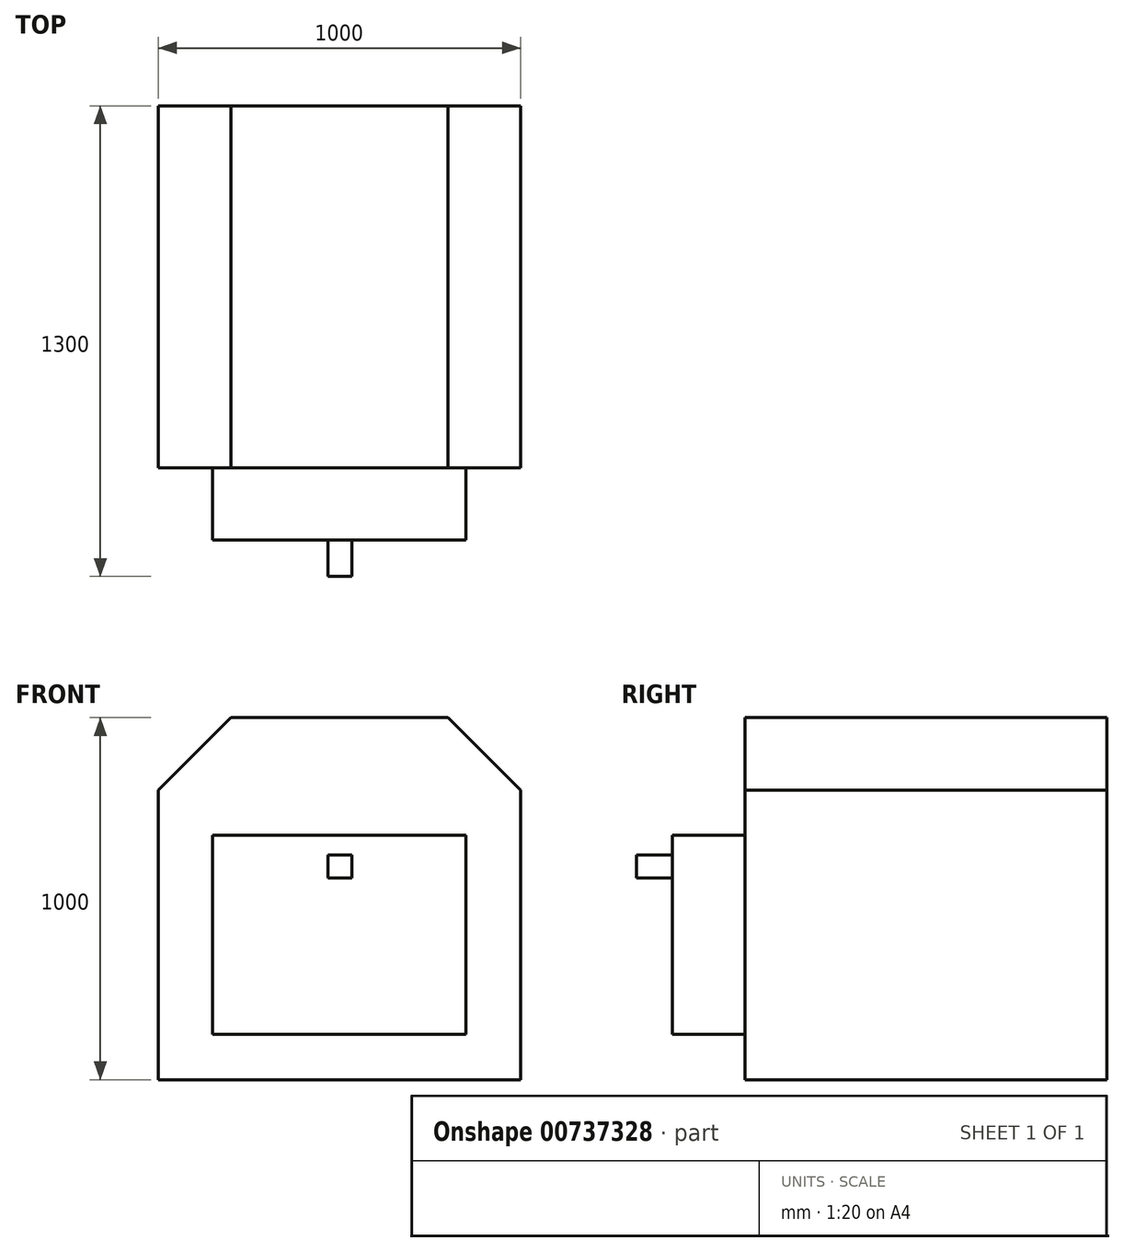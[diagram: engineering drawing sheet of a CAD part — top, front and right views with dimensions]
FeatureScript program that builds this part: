
annotation { "Feature Type Name" : "Feature", "Feature Type Description" : "" }
export const myFeature = defineFeature(function(context is Context, id is Id, definition is map)
    precondition{}
    {
        {
            var Q0;
            Q0=qCreatedBy(makeId("Front.planeOp"),FACE);
            var sketch = newSketch(context, id + "F0", { "sketchPlane" : qUnion([Q0])});
            skLineSegment(sketch, "E0.bottom", {"start": v(-500.63, 675.79) * mm, "end": v(499.37, 675.79) * mm});
            skLineSegment(sketch, "E0.top", {"start": v(-500.63, -324.21) * mm, "end": v(499.37, -324.21) * mm});
            skLineSegment(sketch, "E0.left", {"start": v(-500.63, 675.79) * mm, "end": v(-500.63, -324.21) * mm});
            skLineSegment(sketch, "E0.right", {"start": v(499.37, 675.79) * mm, "end": v(499.37, -324.21) * mm});
            skSolve(sketch);
        }
        {
            var Q0;
            Q0 = qSketchRegion(id + "F0", true);
            extrude(context, id + "F1", {"entities" : qUnion([Q0]), "depth" : 1000 * mm, "offsetDistance" : 25 * mm});
        }
        {
            var Q0;
            Q0=makeQuery(id+"F1.opExtrude","SWEPT_EDGE",EDGE,{"disambiguationData":[OSD([sQuery(id+"F0.wireOp",EDGE,"E0.bottom"),sQuery(id+"F0.wireOp",EDGE,"E0.left")])]});
            var Q1;
            Q1=makeQuery(id+"F1.opExtrude","SWEPT_EDGE",EDGE,{"disambiguationData":[OSD([sQuery(id+"F0.wireOp",EDGE,"E0.bottom"),sQuery(id+"F0.wireOp",EDGE,"E0.right")])]});
            chamfer(context, id + "F2", {"entities" : qUnion([Q0, Q1]), "width" : 200 * mm, "tangentPropagation" : true});
        }
        {
            var Q0;
            Q0=makeQuery(id+"F1.opExtrude","CAP_FACE",FACE,{"disambiguationData":[OSD([sQuery(id+"F0.wireOp",EDGE,"E0.bottom"),sQuery(id+"F0.wireOp",EDGE,"E0.top"),sQuery(id+"F0.wireOp",EDGE,"E0.left"),sQuery(id+"F0.wireOp",EDGE,"E0.right")])],"isStart":false});
            var sketch = newSketch(context, id + "F3", { "sketchPlane" : qUnion([Q0])});
            skLineSegment(sketch, "E1.bottom", {"start": v(-350.63, 350.63) * mm, "end": v(349.37, 350.63) * mm});
            skLineSegment(sketch, "E1.top", {"start": v(-350.63, -199.22) * mm, "end": v(349.37, -199.22) * mm});
            skLineSegment(sketch, "E1.left", {"start": v(-350.63, 350.63) * mm, "end": v(-350.63, -199.22) * mm});
            skLineSegment(sketch, "E1.right", {"start": v(349.37, 350.63) * mm, "end": v(349.37, -199.22) * mm});
            skSolve(sketch);
        }
        {
            var Q0;
            Q0 = qSketchRegion(id + "F3", true);
            extrude(context, id + "F4", {"entities" : qUnion([Q0]), "operationType" : NewBodyOperationType.ADD, "depth" : 200 * mm, "offsetDistance" : 25 * mm});
        }
        {
            var Q0;
            Q0=makeQuery(id+"F4.opExtrude","CAP_FACE",FACE,{"disambiguationData":[OSD([sQuery(id+"F3.wireOp",EDGE,"E1.bottom"),sQuery(id+"F3.wireOp",EDGE,"E1.top"),sQuery(id+"F3.wireOp",EDGE,"E1.left"),sQuery(id+"F3.wireOp",EDGE,"E1.right")])],"isStart":false});
            var sketch = newSketch(context, id + "F5", { "sketchPlane" : qUnion([Q0])});
            skLineSegment(sketch, "E2.bottom", {"start": v(-32.4, 296.52) * mm, "end": v(34.32, 296.52) * mm});
            skLineSegment(sketch, "E2.top", {"start": v(-32.4, 232.97) * mm, "end": v(34.32, 232.97) * mm});
            skLineSegment(sketch, "E2.left", {"start": v(-32.4, 296.52) * mm, "end": v(-32.4, 232.97) * mm});
            skLineSegment(sketch, "E2.right", {"start": v(34.32, 296.52) * mm, "end": v(34.32, 232.97) * mm});
            skSolve(sketch);
        }
        {
            var Q0;
            Q0 = qSketchRegion(id + "F5", true);
            extrude(context, id + "F6", {"entities" : qUnion([Q0]), "operationType" : NewBodyOperationType.ADD, "depth" : 100 * mm, "offsetDistance" : 25 * mm});
        }
    });
